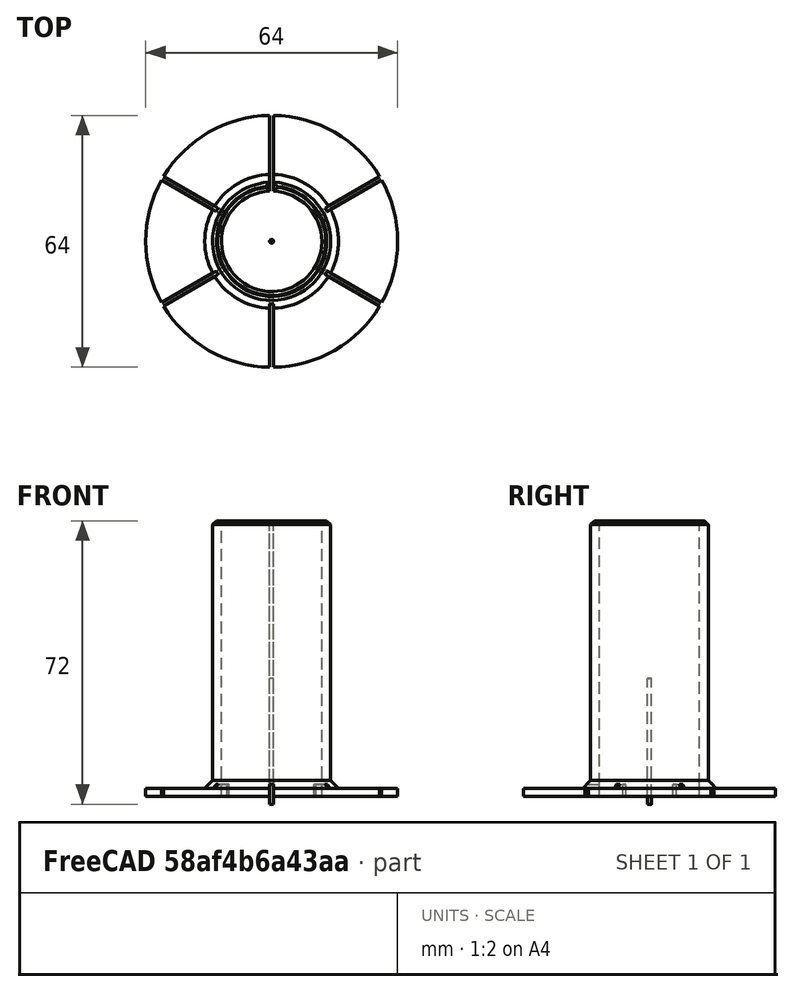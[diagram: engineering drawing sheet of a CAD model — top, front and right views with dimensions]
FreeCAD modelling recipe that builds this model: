
FCSTD DOCUMENT  (FreeCAD 0.17R10665 (Git))
Label: filamenthalter_tube
License: CreativeCommons Attribution-ShareAlike
LicenseURL: http://creativecommons.org/licenses/by-sa/4.0/
objects: Part::Cut×5, Part::Cylinder×4, Part::Box×4, Part::Cone×1, Part::MultiFuse×1, Part::Chamfer×1
note: 16 computed .brp shape members not serialized (recipe doc carries the construction recipe); baked Part::Feature solids carry a one-line shape summary decoded from their .brp

FEATURE [Part::Cylinder] Cylinder
  Angle = 360
  AttacherType = Attacher::AttachEngine3D
  Height = 80
  Placement = pos=(0,0,-1) rot=(0,0,1;0rad)
  Radius = 12.75
FEATURE [Part::Cylinder] Cylinder001
  Angle = 360
  AttacherType = Attacher::AttachEngine3D
  Height = 70
  Radius = 15
FEATURE [Part::Cylinder] Cylinder002  label="ring"
  Angle = 360
  AttacherType = Attacher::AttachEngine3D
  Height = 2
  Radius = 32
FEATURE [Part::Box] Box  label="long cut"
  AttacherType = Attacher::AttachEngine3D
  Height = 80
  Length = 1
  Placement = pos=(-0.5,10,-1) rot=(0,0,1;0rad)
  Width = 24
FEATURE [Part::Box] Box001  label="ring-cut 3"
  AttacherType = Attacher::AttachEngine3D
  Height = 4
  Length = 1
  Placement = pos=(40,-23.67,-1) rot=(0,0,1;1.0472rad)
  Width = 80
FEATURE [Part::Box] Box003  label="ring cut 1"
  AttacherType = Attacher::AttachEngine3D
  Height = 4
  Length = 1
  Placement = pos=(-0.5,-34,-1) rot=(0,0,1;0rad)
  Width = 70
FEATURE [Part::Cylinder] Cylinder003  label="center-pin"
  Angle = 360
  AttacherType = Attacher::AttachEngine3D
  Height = 32
  Placement = pos=(0,0,-2) rot=(0,0,1;0rad)
  Radius = 0.5
FEATURE [Part::Box] Box004  label="ring cut 2"
  AttacherType = Attacher::AttachEngine3D
  Height = 4
  Length = 1
  Placement = pos=(-40,-22.52,-1) rot=(0,0,-1;1.0472rad)
  Width = 80
FEATURE [Part::Cone] Cone
  Angle = 360
  AttacherType = Attacher::AttachEngine3D
  Height = 5
  Radius1 = 19
  Radius2 = 14
FEATURE [Part::MultiFuse] Fusion
  Shapes = -> [Cylinder001,Cylinder002,Cone]
FEATURE [Part::Cut] Cut
  Base = -> Fusion
  Tool = -> Cylinder
FEATURE [Part::Cut] Cut001
  Base = -> Cut
  Tool = -> Box
FEATURE [Part::Cut] Cut002
  Base = -> Cut001
  Tool = -> Box003
FEATURE [Part::Cut] Cut003
  Base = -> Cut002
  Tool = -> Box004
FEATURE [Part::Cut] Cut004
  Base = -> Cut003
  Tool = -> Box001
FEATURE [Part::Chamfer] Chamfer
  Base = -> Cut004
  Edges = 6 edges r=1: [Edge1,Edge2,Edge3,Edge4,Edge5,Edge6]
